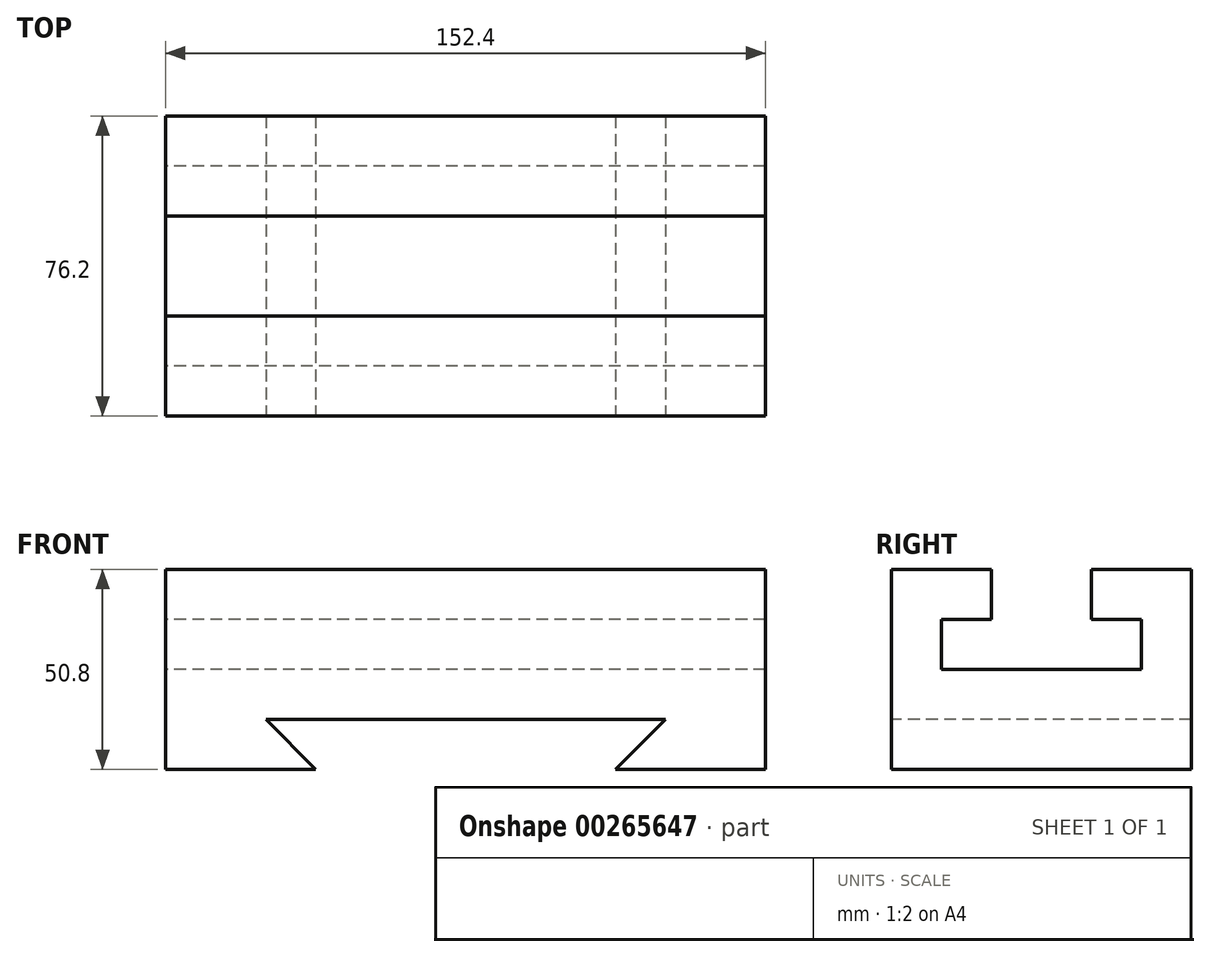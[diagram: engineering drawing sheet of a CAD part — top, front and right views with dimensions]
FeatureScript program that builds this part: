
annotation { "Feature Type Name" : "Feature", "Feature Type Description" : "" }
export const myFeature = defineFeature(function(context is Context, id is Id, definition is map)
    precondition{}
    {
        {
            var Q0;
            Q0=qCreatedBy(makeId("Right.planeOp"),FACE);
            var sketch = newSketch(context, id + "F0", { "sketchPlane" : qUnion([Q0])});
            skLineSegment(sketch, "E0", {"start": v(0, 50.8) * mm, "end": v(0, 0) * mm});
            skLineSegment(sketch, "E1", {"start": v(0, 0) * mm, "end": v(76.2, 0) * mm});
            skLineSegment(sketch, "E2", {"start": v(76.2, 0) * mm, "end": v(76.2, 50.8) * mm});
            skLineSegment(sketch, "E3", {"start": v(0, 50.8) * mm, "end": v(25.4, 50.8) * mm});
            skLineSegment(sketch, "E4", {"start": v(25.4, 50.8) * mm, "end": v(25.4, 38.1) * mm});
            skLineSegment(sketch, "E5", {"start": v(25.4, 38.1) * mm, "end": v(12.7, 38.1) * mm});
            skLineSegment(sketch, "E6", {"start": v(12.7, 38.1) * mm, "end": v(12.7, 25.4) * mm});
            skLineSegment(sketch, "E7", {"start": v(12.7, 25.4) * mm, "end": v(63.5, 25.4) * mm});
            skLineSegment(sketch, "E8", {"start": v(76.2, 50.8) * mm, "end": v(50.8, 50.8) * mm});
            skLineSegment(sketch, "E9", {"start": v(50.8, 50.8) * mm, "end": v(50.8, 38.1) * mm});
            skLineSegment(sketch, "E10", {"start": v(50.8, 38.1) * mm, "end": v(63.5, 38.1) * mm});
            skLineSegment(sketch, "E11", {"start": v(63.5, 38.1) * mm, "end": v(63.5, 25.4) * mm});
            skSolve(sketch);
        }
        {
            var Q0;
            Q0=makeQuery(id+"F0.imprint","IMPRINT",FACE,{"disambiguationData":[TD([[makeQuery(id+"F0.imprint","IMPRINT",EDGE,{"derivedFrom":sQuery(id+"F0.wireOp",EDGE,"E0")}),1.0]])]});
            extrude(context, id + "F1", {"entities" : qUnion([Q0]), "depth" : 152.4 * mm});
        }
        {
            var Q0;
            Q0=makeQuery(id+"F1.opExtrude","SWEPT_FACE",FACE,{"disambiguationData":[OSD([sQuery(id+"F0.wireOp",EDGE,"E0")])]});
            var sketch = newSketch(context, id + "F2", { "sketchPlane" : qUnion([Q0])});
            skLineSegment(sketch, "E12", {"start": v(0, 0) * mm, "end": v(0, 12.7) * mm, "construction": true});
            skLineSegment(sketch, "E13", {"start": v(152.4, 12.7) * mm, "end": v(127, 12.7) * mm, "construction": true});
            skLineSegment(sketch, "E14", {"start": v(127, 12.7) * mm, "end": v(114.3, 0) * mm});
            skLineSegment(sketch, "E15", {"start": v(0, 12.7) * mm, "end": v(25.49, 12.7) * mm, "construction": true});
            skLineSegment(sketch, "E16", {"start": v(25.49, 12.7) * mm, "end": v(38.1, 0) * mm});
            skLineSegment(sketch, "E17", {"start": v(25.49, 12.7) * mm, "end": v(127, 12.7) * mm});
            skLineSegment(sketch, "E18", {"start": v(38.1, 0) * mm, "end": v(38.1, 12.7) * mm, "construction": true});
            skLineSegment(sketch, "E19", {"start": v(38.1, 0) * mm, "end": v(114.3, 0) * mm});
            skSolve(sketch);
        }
        {
            var Q0;
            Q0=makeQuery(id+"F2.imprint","IMPRINT",FACE,{"disambiguationData":[TD([[makeQuery(id+"F2.imprint","IMPRINT",EDGE,{"derivedFrom":sQuery(id+"F2.wireOp",EDGE,"E14")}),-1.0]])]});
            extrude(context, id + "F3", {"entities" : qUnion([Q0]), "operationType" : NewBodyOperationType.REMOVE, "endBound" : BoundingType.UP_TO_NEXT, "oppositeDirection" : true, "depth" : 25.4 * mm});
        }
    });
